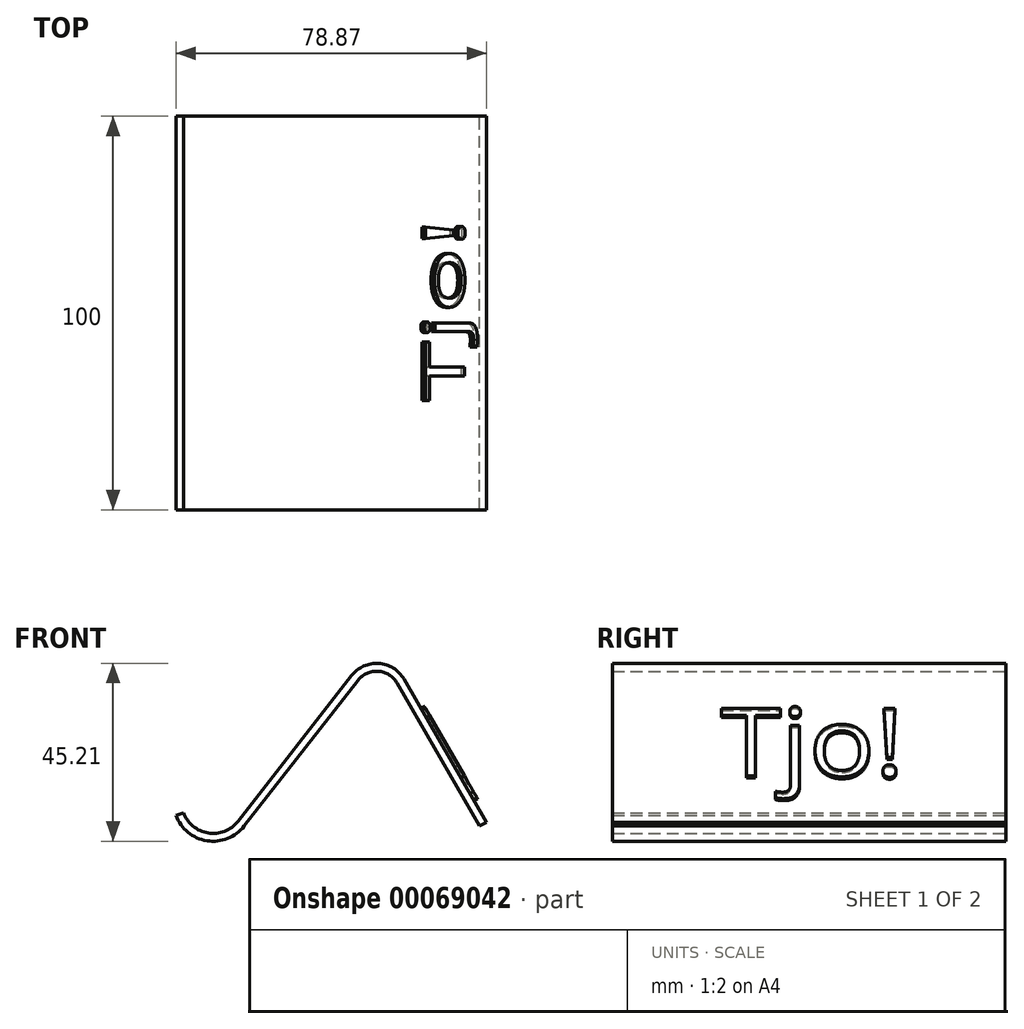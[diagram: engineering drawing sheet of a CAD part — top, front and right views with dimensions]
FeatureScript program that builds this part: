
annotation { "Feature Type Name" : "Feature", "Feature Type Description" : "" }
export const myFeature = defineFeature(function(context is Context, id is Id, definition is map)
    precondition{}
    {
        {
            var Q0;
            Q0=qCreatedBy(makeId("Front.planeOp"),FACE);
            var sketch = newSketch(context, id + "F0", { "sketchPlane" : qUnion([Q0])});
            skLineSegment(sketch, "E0", {"start": v(-34.4, 0) * mm, "end": v(-5.47, 37.05) * mm});
            skLineSegment(sketch, "E1", {"start": v(4.45, 36.36) * mm, "end": v(25.47, 0) * mm});
            skPoint(sketch, "E2.visualSharp", {"position": v(0, 44.06) * mm});
            skArc(sketch, "E2.filletArc", {"start": v(4.45, 36.36) * mm, "mid": v(-0.33, 39.35) * mm, "end": v(-5.47, 37.05) * mm});
            skLineSegment(sketch, "E3.0", {"start": v(6.18, 37.36) * mm, "end": v(27.2, 1) * mm});
            skArc(sketch, "E3.1", {"start": v(6.18, 37.36) * mm, "mid": v(-0.19, 41.34) * mm, "end": v(-7.05, 38.28) * mm});
            skLineSegment(sketch, "E3.2", {"start": v(-35.97, 1.23) * mm, "end": v(-7.05, 38.28) * mm});
            skLineSegment(sketch, "E4", {"start": v(27.2, 1) * mm, "end": v(25.47, 0) * mm});
            skArc(sketch, "E5", {"start": v(-49.8, 3.42) * mm, "mid": v(-43.53, -1.75) * mm, "end": v(-35.97, 1.23) * mm});
            skArc(sketch, "E6.0", {"start": v(-51.67, 2.74) * mm, "mid": v(-43.84, -3.72) * mm, "end": v(-34.4, 0) * mm});
            skLineSegment(sketch, "E7", {"start": v(-49.8, 3.42) * mm, "end": v(-51.67, 2.74) * mm});
            skSolve(sketch);
        }
        {
            var Q0;
            Q0=makeQuery(id+"F0.imprint","IMPRINT",FACE,{"disambiguationData":[TD([[makeQuery(id+"F0.imprint","IMPRINT",EDGE,{"derivedFrom":sQuery(id+"F0.wireOp",EDGE,"E0")}),1.0]])]});
            extrude(context, id + "F1", {"entities" : qUnion([Q0]), "depth" : 100 * mm});
        }
        {
            var Q0;
            Q0=makeQuery(id+"F1.opExtrude","SWEPT_FACE",FACE,{"disambiguationData":[OSD([sQuery(id+"F0.wireOp",EDGE,"E3.0")])]});
            var sketch = newSketch(context, id + "F2", { "sketchPlane" : qUnion([Q0])});
            skText(sketch, "E8", { "text": "Tjo!", "fontName": "OpenSans-Regular.ttf"});
            const initialGuessF2  = {"E8": [-0.0725, 0.00025, 1, 0, 0.02]};
            skSetInitialGuess(sketch, initialGuessF2);
            skSolve(sketch);
        }
        {
            var Q0;
            Q0 = qSketchRegion(id + "F2", true);
            extrude(context, id + "F3", {"entities" : qUnion([Q0]), "operationType" : NewBodyOperationType.ADD, "depth" : 1 * mm});
        }
    });
